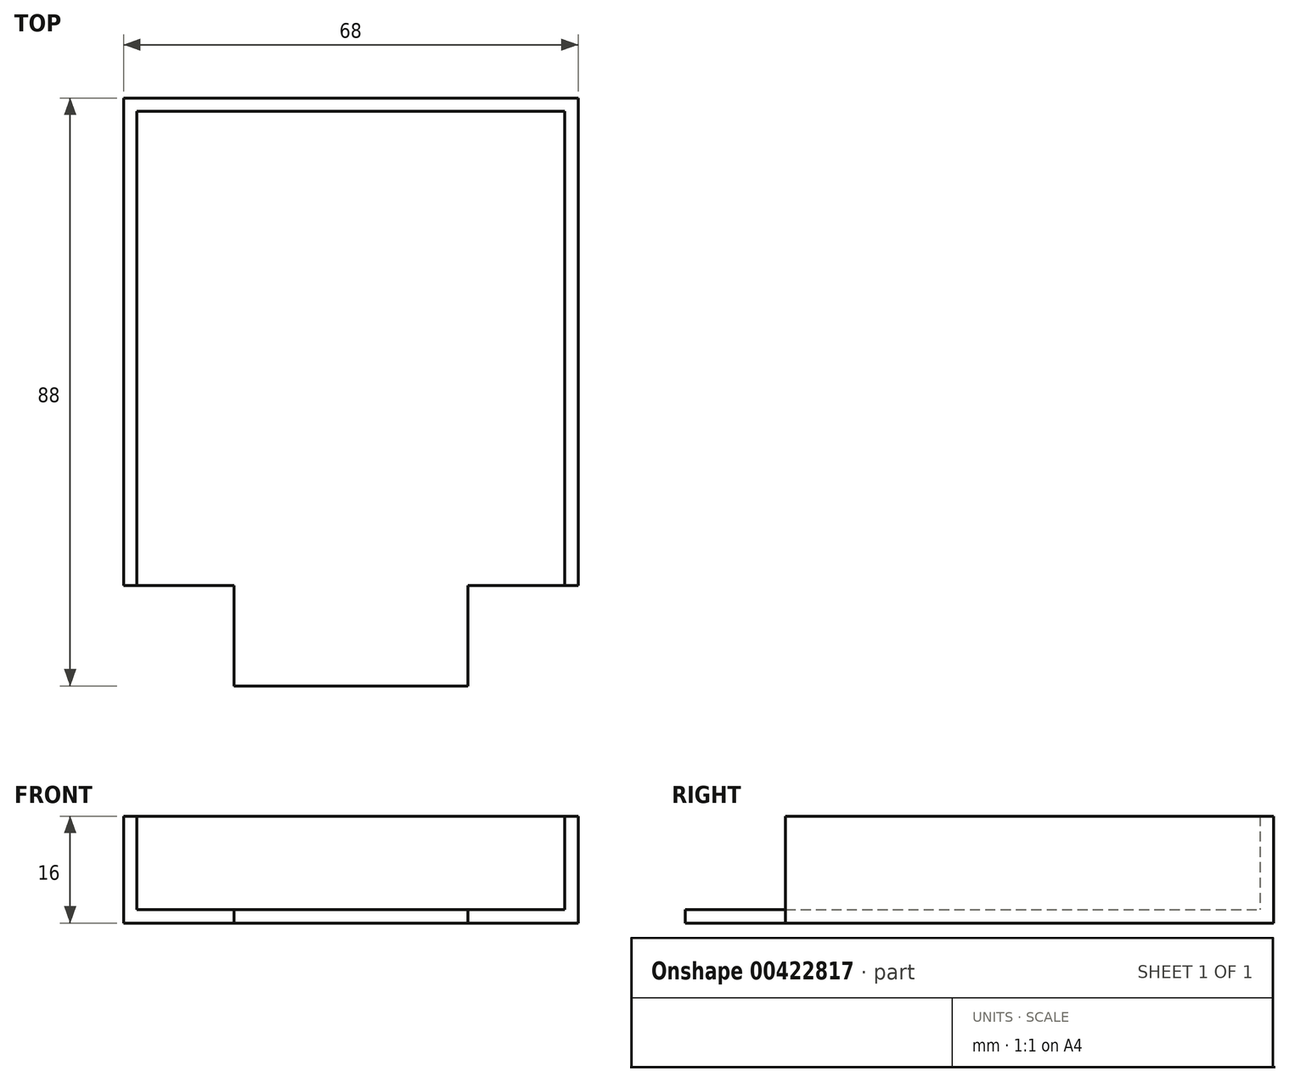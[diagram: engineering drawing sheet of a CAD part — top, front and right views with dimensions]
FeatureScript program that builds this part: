
annotation { "Feature Type Name" : "Feature", "Feature Type Description" : "" }
export const myFeature = defineFeature(function(context is Context, id is Id, definition is map)
    precondition{}
    {
        {
            var Q0;
            Q0=qCreatedBy(makeId("Top.planeOp"),FACE);
            var sketch = newSketch(context, id + "F0", { "sketchPlane" : qUnion([Q0])});
            skLineSegment(sketch, "E0.bottom", {"start": v(0, 0) * mm, "end": v(68, 0) * mm});
            skLineSegment(sketch, "E0.top", {"start": v(0, 73) * mm, "end": v(68, 73) * mm});
            skLineSegment(sketch, "E0.left", {"start": v(0, 0) * mm, "end": v(0, 73) * mm});
            skLineSegment(sketch, "E0.right", {"start": v(68, 0) * mm, "end": v(68, 73) * mm});
            skLineSegment(sketch, "E1.bottom", {"start": v(16.5, 0) * mm, "end": v(51.5, 0) * mm});
            skLineSegment(sketch, "E1.top", {"start": v(16.5, -15) * mm, "end": v(51.5, -15) * mm});
            skLineSegment(sketch, "E1.left", {"start": v(16.5, 0) * mm, "end": v(16.5, -15) * mm});
            skLineSegment(sketch, "E1.right", {"start": v(51.5, 0) * mm, "end": v(51.5, -15) * mm});
            skSolve(sketch);
        }
        {
            var Q0;
            Q0 = qSketchRegion(id + "F0", true);
            extrude(context, id + "F1", {"entities" : qUnion([Q0]), "depth" : 2 * mm});
        }
        {
            var Q0;
            Q0=makeQuery(id+"F1.opExtrude","CAP_FACE",FACE,{"disambiguationData":[OSD([sQuery(id+"F0.wireOp",EDGE,"E0.bottom"),sQuery(id+"F0.wireOp",EDGE,"E0.top"),sQuery(id+"F0.wireOp",EDGE,"E0.left"),sQuery(id+"F0.wireOp",EDGE,"E0.right")])],"isStart":false});
            var sketch = newSketch(context, id + "F2", { "sketchPlane" : qUnion([Q0])});
            skLineSegment(sketch, "E2.bottom", {"start": v(0, 0) * mm, "end": v(2, 0) * mm});
            skLineSegment(sketch, "E2.top", {"start": v(0, 73) * mm, "end": v(2, 73) * mm});
            skLineSegment(sketch, "E2.left", {"start": v(0, 0) * mm, "end": v(0, 73) * mm});
            skLineSegment(sketch, "E2.right", {"start": v(2, 0) * mm, "end": v(2, 73) * mm});
            skLineSegment(sketch, "E3.bottom", {"start": v(68, 0) * mm, "end": v(66, 0) * mm});
            skLineSegment(sketch, "E3.top", {"start": v(68, 73) * mm, "end": v(66, 73) * mm});
            skLineSegment(sketch, "E3.left", {"start": v(68, 0) * mm, "end": v(68, 73) * mm});
            skLineSegment(sketch, "E3.right", {"start": v(66, 0) * mm, "end": v(66, 73) * mm});
            skLineSegment(sketch, "E4.bottom", {"start": v(2, 73) * mm, "end": v(66, 73) * mm});
            skLineSegment(sketch, "E4.top", {"start": v(2, 71) * mm, "end": v(66, 71) * mm});
            skLineSegment(sketch, "E4.left", {"start": v(2, 73) * mm, "end": v(2, 71) * mm});
            skLineSegment(sketch, "E4.right", {"start": v(66, 73) * mm, "end": v(66, 71) * mm});
            skSolve(sketch);
        }
        {
            var Q0;
            Q0 = qSketchRegion(id + "F2", true);
            extrude(context, id + "F3", {"entities" : qUnion([Q0]), "operationType" : NewBodyOperationType.ADD, "depth" : 14 * mm});
        }
    });
